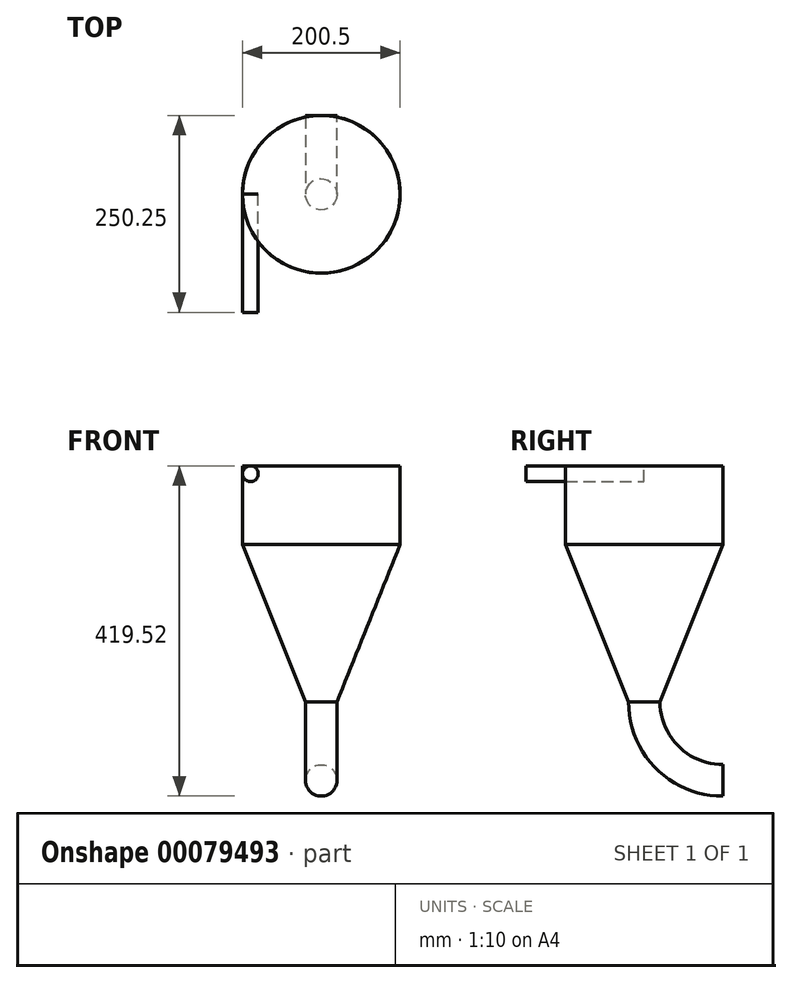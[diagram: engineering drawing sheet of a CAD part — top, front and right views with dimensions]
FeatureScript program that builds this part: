
annotation { "Feature Type Name" : "Feature", "Feature Type Description" : "" }
export const myFeature = defineFeature(function(context is Context, id is Id, definition is map)
    precondition{}
    {
        {
            var Q0;
            Q0=qCreatedBy(makeId("Top.planeOp"),FACE);
            var sketch = newSketch(context, id + "F0", { "sketchPlane" : qUnion([Q0])});
            skCircle(sketch, "E0", {"center": v(0, 0) * mm, "radius": 100 * mm});
            skSolve(sketch);
        }
        {
            var Q0;
            Q0=makeQuery(id+"F0.imprint","IMPRINT",FACE,{"disambiguationData":[TD([[makeQuery(id+"F0.imprint","IMPRINT",EDGE,{"derivedFrom":sQuery(id+"F0.wireOp",EDGE,"E0")}),1.0]])]});
            extrude(context, id + "F1", {"entities" : qUnion([Q0]), "depth" : 100 * mm});
        }
        {
            var Q0;
            Q0=qCreatedBy(makeId("Front.planeOp"),FACE);
            var sketch = newSketch(context, id + "F2", { "sketchPlane" : qUnion([Q0])});
            skCircle(sketch, "E1", {"center": v(-90, 90) * mm, "radius": 10 * mm});
            skSolve(sketch);
        }
        {
            var Q0;
            Q0=makeQuery(id+"F2.imprint","IMPRINT",FACE,{"disambiguationData":[TD([[makeQuery(id+"F2.imprint","IMPRINT",EDGE,{"derivedFrom":sQuery(id+"F2.wireOp",EDGE,"E1")}),1.0]])]});
            extrude(context, id + "F3", {"entities" : qUnion([Q0]), "depth" : 150 * mm});
        }
        {
            var Q0;
            Q0=qCreatedBy(makeId("Front.planeOp"),FACE);
            var sketch = newSketch(context, id + "F4", { "sketchPlane" : qUnion([Q0])});
            skLineSegment(sketch, "E2", {"start": v(0, 0) * mm, "end": v(0, -200) * mm});
            skLineSegment(sketch, "E3", {"start": v(20, -200) * mm, "end": v(100.25, 0) * mm});
            skLineSegment(sketch, "E4", {"start": v(100.25, 0) * mm, "end": v(0, 0) * mm});
            skLineSegment(sketch, "E5", {"start": v(0, -200) * mm, "end": v(20, -200) * mm});
            skSolve(sketch);
        }
        {
            var Q0;
            Q0=makeQuery(id+"F4.imprint","IMPRINT",FACE,{"disambiguationData":[TD([[makeQuery(id+"F4.imprint","IMPRINT",EDGE,{"derivedFrom":sQuery(id+"F4.wireOp",EDGE,"E2")}),1.0]])]});
            var Q1;
            Q1=sQuery(id+"F4.wireOp",EDGE,"E2");
            revolve(context, id + "F5", {"operationType" : NewBodyOperationType.ADD, "entities" : qUnion([Q0]), "axis" : qUnion([Q1]), "revolveType" : RevolveType.FULL});
        }
        {
            var Q0;
            Q0=qCreatedBy(makeId("Right.planeOp"),FACE);
            var sketch = newSketch(context, id + "F6", { "sketchPlane" : qUnion([Q0])});
            skArc(sketch, "E6", {"start": v(0, -199.52) * mm, "mid": v(29.29, -270.23) * mm, "end": v(100, -299.52) * mm});
            skPoint(sketch, "E7.start.orphan", {"position": v(0, -199.52) * mm});
            skSolve(sketch);
        }
        {
            var Q0;
            Q0=makeQuery(id+"F5.opRevolve","SWEPT_FACE",FACE,{"disambiguationData":[OSD([sQuery(id+"F4.wireOp",EDGE,"E5")])]});
            var Q1;
            Q1=sQuery(id+"F6.wireOp",EDGE,"E6");
            sweep(context, id + "F7", {"operationType" : NewBodyOperationType.ADD, "profiles" : qUnion([Q0]), "path" : qUnion([Q1])});
        }
    });
